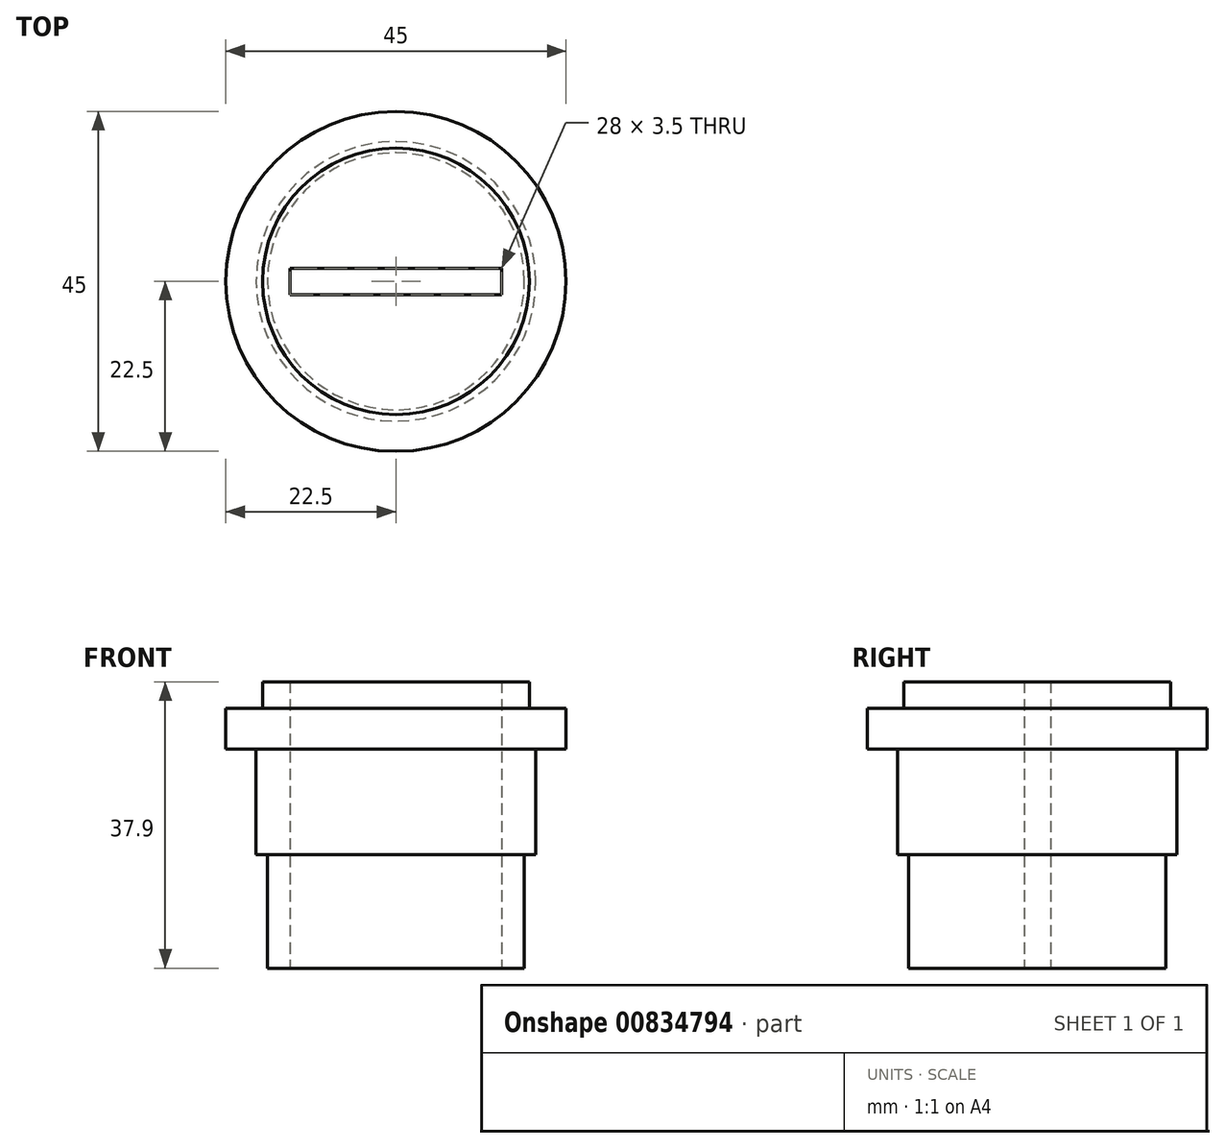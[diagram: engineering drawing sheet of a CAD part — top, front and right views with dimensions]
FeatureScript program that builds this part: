
annotation { "Feature Type Name" : "Feature", "Feature Type Description" : "" }
export const myFeature = defineFeature(function(context is Context, id is Id, definition is map)
    precondition{}
    {
        {
            var Q0;
            Q0=qCreatedBy(makeId("Front.planeOp"),FACE);
            var sketch = newSketch(context, id + "F0", { "sketchPlane" : qUnion([Q0])});
            skLineSegment(sketch, "E0", {"start": v(0, 0) * mm, "end": v(18.5, 0) * mm});
            skLineSegment(sketch, "E1", {"start": v(18.5, 0) * mm, "end": v(18.5, 14) * mm});
            skLineSegment(sketch, "E2", {"start": v(18.5, 14) * mm, "end": v(22.5, 14) * mm});
            skLineSegment(sketch, "E3", {"start": v(22.5, 14) * mm, "end": v(22.5, 19.4) * mm});
            skLineSegment(sketch, "E4", {"start": v(22.5, 19.4) * mm, "end": v(17.64, 19.4) * mm});
            skLineSegment(sketch, "E5", {"start": v(17.64, 19.4) * mm, "end": v(17.64, 22.9) * mm});
            skLineSegment(sketch, "E6", {"start": v(17.64, 22.9) * mm, "end": v(0, 22.9) * mm});
            skLineSegment(sketch, "E7", {"start": v(0, -3.12) * mm, "end": v(0, 0) * mm, "construction": true});
            skLineSegment(sketch, "E8", {"start": v(0, 22.9) * mm, "end": v(0, 0) * mm});
            skSolve(sketch);
        }
        {
            var Q0;
            Q0 = qSketchRegion(id + "F0", true);
            var Q1;
            Q1=sQuery(id+"F0.wireOp",EDGE,"E7");
            revolve(context, id + "F1", {"surfaceOperationType" : NewSurfaceOperationType.NEW, "entities" : qUnion([Q0]), "axis" : qUnion([Q1]), "revolveType" : RevolveType.FULL});
        }
        {
            var Q0;
            Q0=makeQuery(id+"F1.opRevolve","SWEPT_FACE",FACE,{"disambiguationData":[OSD([sQuery(id+"F0.wireOp",EDGE,"E0")])]});
            var sketch = newSketch(context, id + "F2", { "sketchPlane" : qUnion([Q0])});
            skCircle(sketch, "E9", {"center": v(0, 0) * mm, "radius": 17 * mm});
            skSolve(sketch);
        }
        {
            var Q0;
            Q0 = qSketchRegion(id + "F2", true);
            extrude(context, id + "F3", {"entities" : qUnion([Q0]), "operationType" : NewBodyOperationType.ADD, "depth" : 15 * mm, "offsetDistance" : 25 * mm});
        }
        {
            var Q0;
            Q0=makeQuery(id+"F3.opExtrude","CAP_FACE",FACE,{"disambiguationData":[OSD([sQuery(id+"F2.wireOp",EDGE,"E9")])],"isStart":false});
            var sketch = newSketch(context, id + "F4", { "sketchPlane" : qUnion([Q0])});
            skLineSegment(sketch, "E10.bottom", {"start": v(-14, 1.75) * mm, "end": v(14, 1.75) * mm});
            skLineSegment(sketch, "E10.top", {"start": v(-14, -1.75) * mm, "end": v(14, -1.75) * mm});
            skLineSegment(sketch, "E10.left", {"start": v(-14, 1.75) * mm, "end": v(-14, -1.75) * mm});
            skLineSegment(sketch, "E10.right", {"start": v(14, 1.75) * mm, "end": v(14, -1.75) * mm});
            skPoint(sketch, "E10.middle", {"position": v(0, 0) * mm});
            skSolve(sketch);
        }
        {
            var Q0;
            Q0 = qSketchRegion(id + "F4", true);
            extrude(context, id + "F5", {"entities" : qUnion([Q0]), "operationType" : NewBodyOperationType.REMOVE, "oppositeDirection" : true, "depth" : 40 * mm, "offsetDistance" : 25 * mm});
        }
    });
